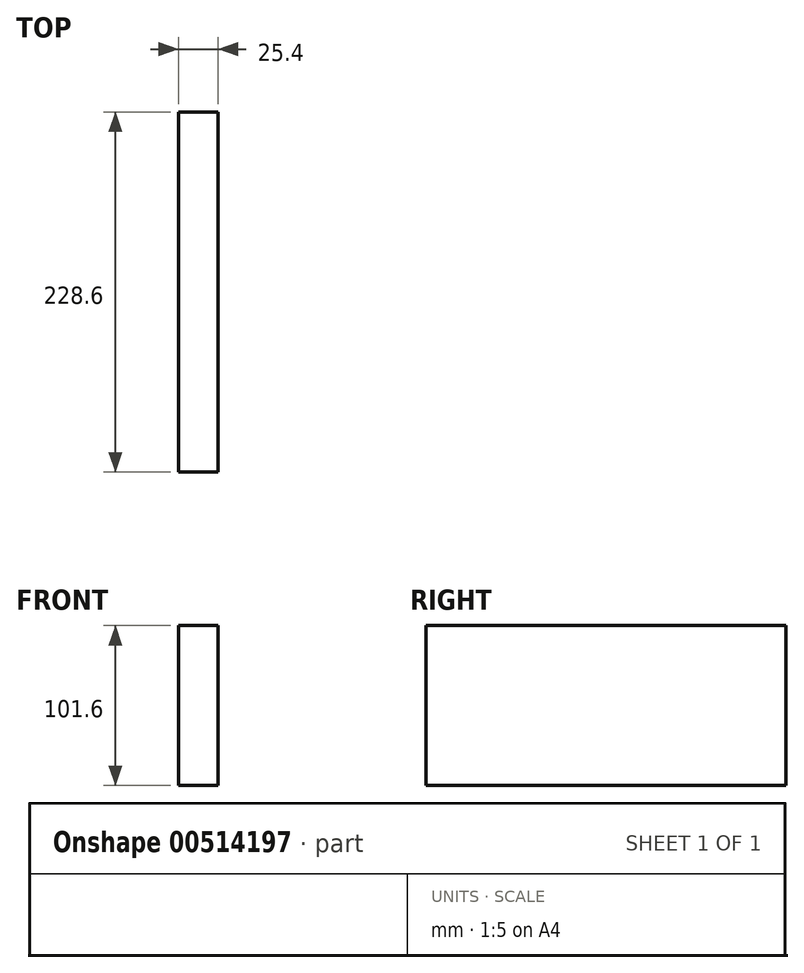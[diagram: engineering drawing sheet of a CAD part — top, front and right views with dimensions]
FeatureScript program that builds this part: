
annotation { "Feature Type Name" : "Feature", "Feature Type Description" : "" }
export const myFeature = defineFeature(function(context is Context, id is Id, definition is map)
    precondition{}
    {
        {
            var Q0;
            Q0=qCreatedBy(makeId("Right.planeOp"),FACE);
            var sketch = newSketch(context, id + "F0", { "sketchPlane" : qUnion([Q0])});
            skLineSegment(sketch, "E0.bottom", {"start": v(-170.37, 118.36) * mm, "end": v(58.23, 118.36) * mm});
            skLineSegment(sketch, "E0.top", {"start": v(-170.37, 16.76) * mm, "end": v(58.23, 16.76) * mm});
            skLineSegment(sketch, "E0.left", {"start": v(-170.37, 118.36) * mm, "end": v(-170.37, 16.76) * mm});
            skLineSegment(sketch, "E0.right", {"start": v(58.23, 118.36) * mm, "end": v(58.23, 16.76) * mm});
            skSolve(sketch);
        }
        {
            var Q0;
            Q0=makeQuery(id+"F0.imprint","IMPRINT",FACE,{"disambiguationData":[TD([[makeQuery(id+"F0.imprint","IMPRINT",EDGE,{"derivedFrom":sQuery(id+"F0.wireOp",EDGE,"E0.bottom")}),-1.0]])]});
            extrude(context, id + "F1", {"entities" : qUnion([Q0]), "depth" : 25.4 * mm, "offsetDistance" : 25.4 * mm});
        }
    });
